# Revit family: BOS-Doppeltürzarge-Oud-MW_Familie
name_source: partatom
category: Türen
revit_build: Autodesk Revit 2017 (Build: 20160225_1515(x64)
units: mm (PartAtom-declared; Revit-internal decimal feet)

## family parameters
Basisbauteil = Wand
Beim Laden mit Abzugskörper schneiden = Nein
Gemeinsam genutzt = Nein
Immer vertikal = Ja
Raumberechnungspunkt = Ja

## types (4) — shared parameters
BBL1 Bandbezugslinie   Hinge Position 1 = 241 mm  [stored 0.790682 ft]
BE max. = 100 mm  [stored 0.328084 ft]
Bauelement = BOS Stahlzarge
Blechstärke = 1.5 mm  [stored 0.00492126 ft]
Dichtung 1 = Ja
Dichtung hinten 1 = Ja
Drehpunkt Warnung sichtbar = Ja
Drehpunktreferenz horizontal = 500 mm  [stored 1.64042 ft]
Drückerhöheunterschied min. = 120 mm  [stored 0.393701 ft]
Drückertiefe = 70 mm  [stored 0.229659 ft]
Einfügepunkt = 37 mm  [stored 0.121391 ft]
FMB max. = 1342 mm  [stored 4.40289 ft]
FMB min. = 591 mm  [stored 1.93898 ft]
FMH max. = 2858 mm
FMH min. = 1608 mm
Falzaufschlag = 15 mm  [stored 0.0492126 ft]
Falztiefe 2 = 25 mm  [stored 0.082021 ft]
Falztiefe hinten 2 = 25 mm  [stored 0.082021 ft]
Funktion = Innen
GT max. = 650 mm  [stored 2.13255 ft]
Hersteller = BOS GmbH Best Of Steel, Lütkenfelde 4, D-48282 Emsdetten
Info-Texte sichtbar = Ja
Information in English = Nein
Leibungstiefe min. = 54 mm  [stored 0.177165 ft]
Material = grundiert, feuerverzinktes Feinblech nach DIN EN 10143
Material - Bänder = <Nach Kategorie>
Material - Dichtung = <Nach Kategorie>
Material - Drückergarnitur = <Nach Kategorie>
Material - Türblatt = <Nach Kategorie>
Material - Zarge = <Nach Kategorie>
Putzwinkel max. = 28 mm  [stored 0.0918635 ft]
Putzwinkel min. = 10 mm  [stored 0.0328084 ft]
Sickentiefe = 10 mm  [stored 0.0328084 ft]
Spiegel hinten max. = 30 mm  [stored 0.0984252 ft]
Spiegel hinten min. = 30 mm  [stored 0.0984252 ft]
Spiegel vorne max. = 80 mm  [stored 0.262467 ft]
Spiegel vorne min. = 30 mm  [stored 0.0984252 ft]
Technische Infos rund um die Stahlzarge = www.BestOfSteel.de/tools-downloads/technische-infos-rund-um-die-stahlzarge/
Typenbild = <Keine Auswahl>
Türblattabstand 2 = 4.5 mm  [stored 0.0147638 ft]
Türblattabstand 3 = 4.5 mm  [stored 0.0147638 ft]
Türblattabstand links-rechts = 3.5 mm  [stored 0.0114829 ft]
Türblattabstand oben = 4 mm  [stored 0.0131234 ft]
Türblattabstand unten = 7 mm  [stored 0.0229659 ft]
Türblattaufschlag = 13 mm
URL = www.BestOfSteel.de/stahlzargen/zargen-fuer-drehfluegeltueren/doppeltuerzargen/
Öffnungswinkel max. = 180.00°
Öffnungswinkel min. = 0.00°
zero-valued in all types: Breite, Dicke, Rohbaubreite, Rohbauhöhe, Türblattabstand zusätzlich

## per-type parameters (varying)
- Oud: Beschreibung=Doppeltürzarge für Mauerwerk, gefälzt; Dichtung 2=Nein; Dichtung hinten 2=Nein; Doppelfalz=Nein; Drehpunkt-hinten-abstand (FM) horizontal=21 mm  [stored 0.0688976 ft]; Drehpunkt-hinten-abstand (SP) vertikal=12.5 mm  [stored 0.0410105 ft]; Drehpunkt-vorne-abstand (FM) horizontal=21 mm  [stored 0.0688976 ft]; Drehpunkt-vorne-abstand (SP) vertikal=12.5 mm  [stored 0.0410105 ft]; Einfachfalz=Ja; Falzaufschlag gesamt=15 mm  [stored 0.0492126 ft]; Falztiefe=28.5 mm  [stored 0.0935039 ft]; Falztiefe gesamt=28.5 mm  [stored 0.0935039 ft]; Falztiefe gesamt hinten=28.5 mm  [stored 0.0935039 ft]; Falztiefe hinten=28.5 mm  [stored 0.0935039 ft]; Gefälzt=Ja; OsFd=Nein; Osd=Nein; OuFd=Nein; Oud=Ja; Stumpf=Nein; Türblattabstand 1=1.5 mm  [stored 0.00492126 ft]; Türblattstärke=40 mm  [stored 0.131234 ft]; Türblattstärke 1=14.5 mm  [stored 0.0475722 ft]; Türblattstärke 2=25.5 mm  [stored 0.0836614 ft]; Türblattstärke 3=0 mm  [stored 0 ft]; Türblattstärke hinten=40 mm  [stored 0.131234 ft]; Türblattstärke hinten 1=14.5 mm  [stored 0.0475722 ft]; Türblattstärke hinten 2=25.5 mm  [stored 0.0836614 ft]; Türblattstärke hinten 3=0 mm  [stored 0 ft]; Türblattversatz  horizontal=11.5 mm  [stored 0.0377297 ft]; Türblattversatz horizontal hinten=11.5 mm  [stored 0.0377297 ft]; Türblattversatz vertikal=-3.5 mm  [stored -0.0114829 ft]; Türblattversatz vertikal hinten=-3.5 mm  [stored -0.0114829 ft]
- OuFd: Beschreibung=Doppeltürzarge für Mauerwerk, gefälzt, mit Doppelfalz; Dichtung 2=Ja; Dichtung hinten 2=Ja; Doppelfalz=Ja; Drehpunkt-hinten-abstand (FM) horizontal=21 mm  [stored 0.0688976 ft]; Drehpunkt-hinten-abstand (SP) vertikal=12.5 mm  [stored 0.0410105 ft]; Drehpunkt-vorne-abstand (FM) horizontal=21 mm  [stored 0.0688976 ft]; Drehpunkt-vorne-abstand (SP) vertikal=12.5 mm  [stored 0.0410105 ft]; Einfachfalz=Nein; Falzaufschlag gesamt=30 mm  [stored 0.0984252 ft]; Falztiefe=28.5 mm  [stored 0.0935039 ft]; Falztiefe gesamt=53.5 mm  [stored 0.175525 ft]; Falztiefe gesamt hinten=53.5 mm  [stored 0.175525 ft]; Falztiefe hinten=28.5 mm  [stored 0.0935039 ft]; Gefälzt=Ja; OsFd=Nein; Osd=Nein; OuFd=Ja; Oud=Nein; Stumpf=Nein; Türblattabstand 1=1.5 mm  [stored 0.00492126 ft]; Türblattstärke=65 mm  [stored 0.213255 ft]; Türblattstärke 1=14.5 mm  [stored 0.0475722 ft]; Türblattstärke 2=25.5 mm  [stored 0.0836614 ft]; Türblattstärke 3=25 mm  [stored 0.082021 ft]; Türblattstärke hinten=65 mm  [stored 0.213255 ft]; Türblattstärke hinten 1=14.5 mm  [stored 0.0475722 ft]; Türblattstärke hinten 2=25.5 mm  [stored 0.0836614 ft]; Türblattstärke hinten 3=25 mm  [stored 0.082021 ft]; Türblattversatz  horizontal=11.5 mm  [stored 0.0377297 ft]; Türblattversatz horizontal hinten=11.5 mm  [stored 0.0377297 ft]; Türblattversatz vertikal=-3.5 mm  [stored -0.0114829 ft]; Türblattversatz vertikal hinten=-3.5 mm  [stored -0.0114829 ft]
- Osd: Beschreibung=Doppeltürzarge für Mauerwerk, stumpf; Dichtung 2=Nein; Dichtung hinten 2=Nein; Doppelfalz=Nein; Drehpunkt-hinten-abstand (FM) horizontal=2.5 mm  [stored 0.0082021 ft]; Drehpunkt-hinten-abstand (SP) vertikal=13.5 mm  [stored 0.0442913 ft]; Drehpunkt-vorne-abstand (FM) horizontal=2.5 mm  [stored 0.0082021 ft]; Drehpunkt-vorne-abstand (SP) vertikal=13.5 mm  [stored 0.0442913 ft]; Einfachfalz=Ja; Falzaufschlag gesamt=15 mm  [stored 0.0492126 ft]; Falztiefe=46.5 mm  [stored 0.152559 ft]; Falztiefe gesamt=46.5 mm  [stored 0.152559 ft]; Falztiefe gesamt hinten=46.5 mm  [stored 0.152559 ft]; Falztiefe hinten=46.5 mm  [stored 0.152559 ft]; Gefälzt=Nein; OsFd=Nein; Osd=Ja; OuFd=Nein; Oud=Nein; Stumpf=Ja; Türblattabstand 1=-2 mm  [stored -0.00656168 ft]; Türblattstärke=40 mm  [stored 0.131234 ft]; Türblattstärke 1=0 mm  [stored 0 ft]; Türblattstärke 2=40 mm  [stored 0.131234 ft]; Türblattstärke 3=0 mm  [stored 0 ft]; Türblattstärke hinten=40 mm  [stored 0.131234 ft]; Türblattstärke hinten 1=0 mm  [stored 0 ft]; Türblattstärke hinten 2=40 mm  [stored 0.131234 ft]; Türblattstärke hinten 3=0 mm  [stored 0 ft]; Türblattversatz  horizontal=6 mm  [stored 0.019685 ft]; Türblattversatz horizontal hinten=6 mm  [stored 0.019685 ft]; Türblattversatz vertikal=15.5 mm  [stored 0.050853 ft]; Türblattversatz vertikal hinten=15.5 mm  [stored 0.050853 ft]
- OsFd: Beschreibung=Doppeltürzarge für Mauerwerk, stumpf, mit Doppelfalz; Dichtung 2=Ja; Dichtung hinten 2=Ja; Doppelfalz=Ja; Drehpunkt-hinten-abstand (FM) horizontal=2.5 mm  [stored 0.0082021 ft]; Drehpunkt-hinten-abstand (SP) vertikal=13.5 mm  [stored 0.0442913 ft]; Drehpunkt-vorne-abstand (FM) horizontal=2.5 mm  [stored 0.0082021 ft]; Drehpunkt-vorne-abstand (SP) vertikal=13.5 mm  [stored 0.0442913 ft]; Einfachfalz=Nein; Falzaufschlag gesamt=30 mm  [stored 0.0984252 ft]; Falztiefe=46.5 mm  [stored 0.152559 ft]; Falztiefe gesamt=71.5 mm; Falztiefe gesamt hinten=71.5 mm; Falztiefe hinten=46.5 mm  [stored 0.152559 ft]; Gefälzt=Nein; OsFd=Ja; Osd=Nein; OuFd=Nein; Oud=Nein; Stumpf=Ja; Türblattabstand 1=-2 mm  [stored -0.00656168 ft]; Türblattstärke=65 mm  [stored 0.213255 ft]; Türblattstärke 1=0 mm  [stored 0 ft]; Türblattstärke 2=40 mm  [stored 0.131234 ft]; Türblattstärke 3=25 mm  [stored 0.082021 ft]; Türblattstärke hinten=65 mm  [stored 0.213255 ft]; Türblattstärke hinten 1=0 mm  [stored 0 ft]; Türblattstärke hinten 2=40 mm  [stored 0.131234 ft]; Türblattstärke hinten 3=25 mm  [stored 0.082021 ft]; Türblattversatz  horizontal=6 mm  [stored 0.019685 ft]; Türblattversatz horizontal hinten=6 mm  [stored 0.019685 ft]; Türblattversatz vertikal=15.5 mm  [stored 0.050853 ft]; Türblattversatz vertikal hinten=15.5 mm  [stored 0.050853 ft]

note: column(s) folded — value = type name in every type: Modell

note: [stored X ft] marks values corroborated as IEEE doubles in the binary element streams (Revit-internal decimal feet)
